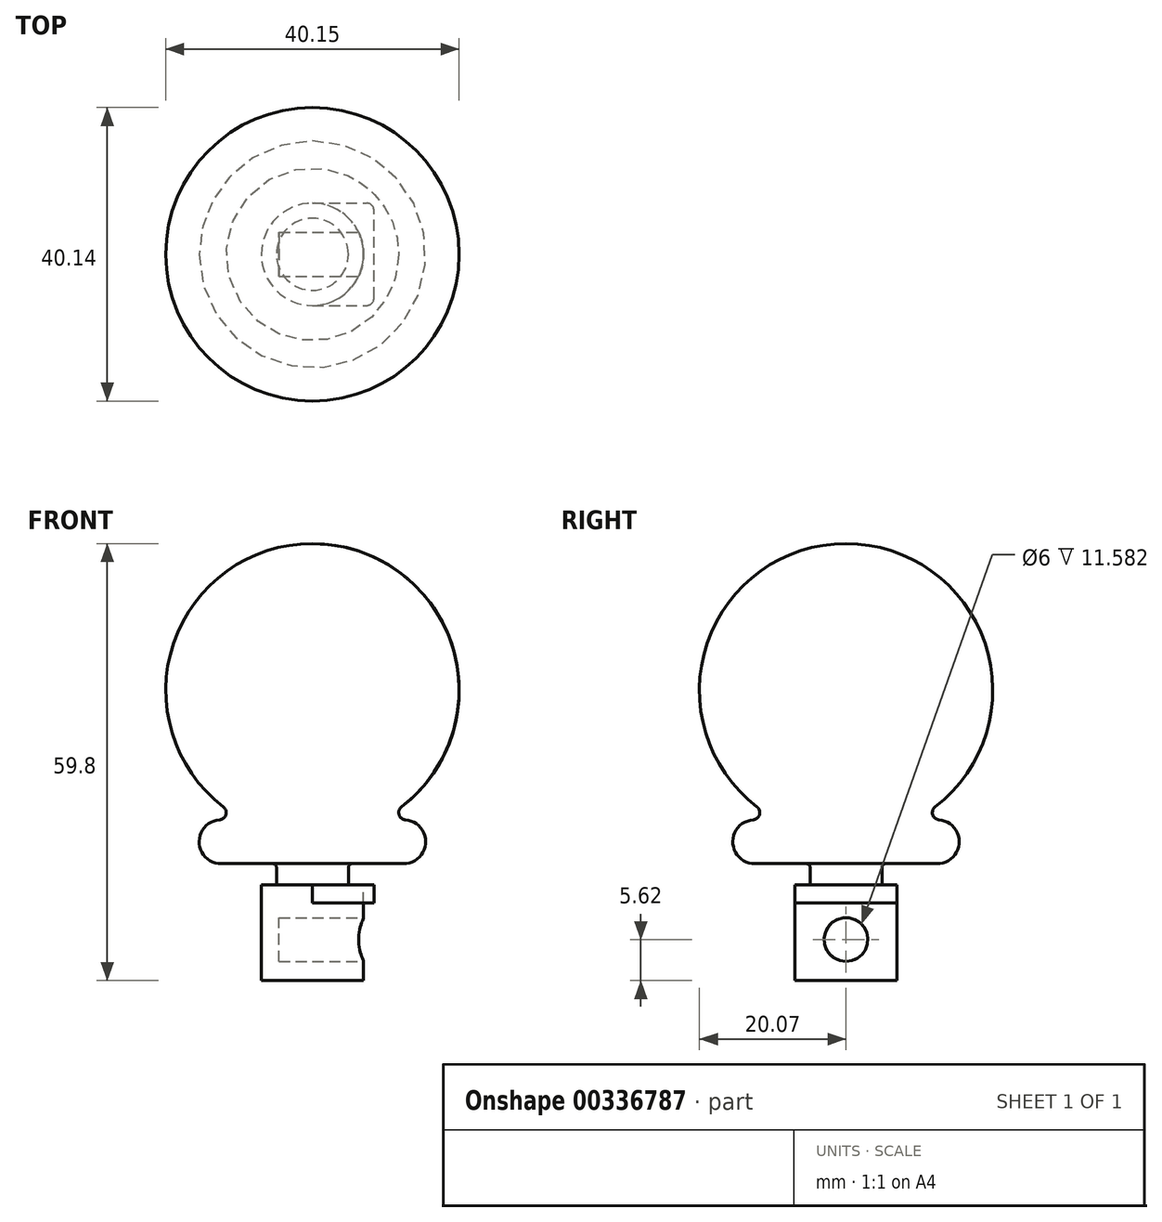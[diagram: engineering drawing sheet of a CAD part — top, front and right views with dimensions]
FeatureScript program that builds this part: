
annotation { "Feature Type Name" : "Feature", "Feature Type Description" : "" }
export const myFeature = defineFeature(function(context is Context, id is Id, definition is map)
    precondition{}
    {
        {
            var Q0;
            Q0=qCreatedBy(makeId("Front.planeOp"),FACE);
            var sketch = newSketch(context, id + "F0", { "sketchPlane" : qUnion([Q0])});
            skLineSegment(sketch, "E0", {"start": v(0, 0) * mm, "end": v(0, 59.8) * mm});
            skArc(sketch, "E1", {"start": v(9.42, 22) * mm, "mid": v(19.48, 44.58) * mm, "end": v(0, 59.8) * mm});
            skLineSegment(sketch, "E2", {"start": v(9.42, 22) * mm, "end": v(15.5, 22) * mm});
            skLineSegment(sketch, "E3", {"start": v(4.92, 16) * mm, "end": v(15.5, 16) * mm});
            skLineSegment(sketch, "E4", {"start": v(15.5, 16) * mm, "end": v(15.5, 22) * mm});
            skLineSegment(sketch, "E5.0", {"start": v(4.92, 13.12) * mm, "end": v(4.92, 16) * mm});
            skLineSegment(sketch, "E6.0", {"start": v(4.92, 13.12) * mm, "end": v(7, 13.12) * mm});
            skLineSegment(sketch, "E7.0", {"start": v(7, 0) * mm, "end": v(7, 13.12) * mm});
            skLineSegment(sketch, "E8", {"start": v(0, 0) * mm, "end": v(7, 0) * mm});
            skSolve(sketch);
        }
        {
            var Q0;
            Q0 = qSketchRegion(id + "F0", true);
            var Q1;
            Q1=sQuery(id+"F0.wireOp",EDGE,"E0");
            revolve(context, id + "F1", {"entities" : qUnion([Q0]), "axis" : qUnion([Q1]), "revolveType" : RevolveType.FULL});
        }
        {
            var Q0;
            Q0=makeQuery(id+"F1.opRevolve","SWEPT_FACE",FACE,{"disambiguationData":[OSD([sQuery(id+"F0.wireOp",EDGE,"E6.0")])]});
            var sketch = newSketch(context, id + "F2", { "sketchPlane" : qUnion([Q0])});
            skLineSegment(sketch, "E9", {"start": v(0, -7) * mm, "end": v(8.42, -7) * mm});
            skLineSegment(sketch, "E10.MirrorCS", {"start": v(0, 7) * mm, "end": v(8.42, 7) * mm});
            skLineSegment(sketch, "E11", {"start": v(8.42, -7) * mm, "end": v(8.42, 7) * mm});
            skArc(sketch, "E12.0", {"start": v(0, -7) * mm, "mid": v(7, 0) * mm, "end": v(0, 7) * mm});
            skSolve(sketch);
        }
        {
            var Q0;
            Q0 = qSketchRegion(id + "F2", true);
            extrude(context, id + "F3", {"entities" : qUnion([Q0]), "oppositeDirection" : true, "depth" : 2.5 * mm});
        }
        {
            var Q0;
            Q0=makeQuery(id+"F3.opExtrude","SWEPT_FACE",FACE,{"disambiguationData":[OSD([sQuery(id+"F2.wireOp",EDGE,"E11")])]});
            var sketch = newSketch(context, id + "F4", { "sketchPlane" : qUnion([Q0])});
            skLineSegment(sketch, "E13.0", {"start": v(7, 5.62) * mm, "end": v(-7, 5.62) * mm});
            skCircle(sketch, "E14", {"center": v(0, 5.62) * mm, "radius": 3 * mm});
            skSolve(sketch);
        }
        {
            var Q0;
            Q0 = qSketchRegion(id + "F4", true);
            extrude(context, id + "F5", {"entities" : qUnion([Q0]), "operationType" : NewBodyOperationType.REMOVE, "oppositeDirection" : true, "depth" : 13 * mm});
        }
        {
            var Q0;
            Q0=makeQuery(id+"F1.opRevolve","SWEPT_EDGE",EDGE,{"disambiguationData":[OSD([sQuery(id+"F0.wireOp",EDGE,"E2"),sQuery(id+"F0.wireOp",EDGE,"E4")])]});
            var Q1;
            Q1=makeQuery(id+"F1.opRevolve","SWEPT_EDGE",EDGE,{"disambiguationData":[OSD([sQuery(id+"F0.wireOp",EDGE,"E3"),sQuery(id+"F0.wireOp",EDGE,"E4")])]});
            fillet(context, id + "F6", {"entities" : qUnion([Q0, Q1]), "radius" : 3 * mm, "tangentPropagation" : true, "allowEdgeOverflow" : false});
        }
        {
            var Q0;
            Q0=makeQuery(id+"F1.opRevolve","SWEPT_EDGE",EDGE,{"disambiguationData":[OSD([sQuery(id+"F0.wireOp",EDGE,"E1"),sQuery(id+"F0.wireOp",EDGE,"E2")])]});
            fillet(context, id + "F7", {"entities" : qUnion([Q0]), "radius" : 1 * mm, "tangentPropagation" : true, "allowEdgeOverflow" : false});
        }
        {
            var Q0;
            Q0=makeQuery(id+"F3.opExtrude","SWEPT_EDGE",EDGE,{"disambiguationData":[OSD([sQuery(id+"F2.wireOp",EDGE,"E9"),sQuery(id+"F2.wireOp",EDGE,"E11")])]});
            var Q1;
            Q1=makeQuery(id+"F3.opExtrude","SWEPT_EDGE",EDGE,{"disambiguationData":[OSD([sQuery(id+"F2.wireOp",EDGE,"E10.MirrorCS"),sQuery(id+"F2.wireOp",EDGE,"E11")])]});
            fillet(context, id + "F8", {"entities" : qUnion([Q0, Q1]), "radius" : 1 * mm, "tangentPropagation" : true, "allowEdgeOverflow" : false});
        }
        {
            var Q0;
            Q0=makeQuery(id+"F1.opRevolve","SWEPT_EDGE",EDGE,{"disambiguationData":[OSD([sQuery(id+"F0.wireOp",EDGE,"E3"),sQuery(id+"F0.wireOp",EDGE,"E5.0")])]});
            fillet(context, id + "F9", {"entities" : qUnion([Q0]), "radius" : .5 * mm, "tangentPropagation" : true, "allowEdgeOverflow" : false});
        }
    });
